# Revit family: Krome C8863-C8868 VS seris
name_source: partatom
category: Generic Models
revit_build: Autodesk Revit 2018 (Build: 20170223_1515(x64)
units: mm (PartAtom-declared; Revit-internal decimal feet)

## family parameters
Always vertical = Yes
Can host rebar = No
Cut with Voids When Loaded = No
Part Type = Normal
Room Calculation Point = No
Round Connector Dimension = Use Diameter
Shared = No
Work Plane-Based = No

## types (6) — shared parameters
Model = C8863-VS Series
URL = http://www.kromedispense.com

## per-type parameters (varying)
| type | Weight (lbs.) |
| C8864-VS-12" Ecoline Wall Mount Grab Bar Vibrant Stainless | 1.29 |
| C8863-VS-9" Ecoline Wall Mount Grab Bar Vibrant Stainless | 1.20 |
| C8865-VS-18" Ecoline Wall Mount Grab Bar Vibrant Stainless | 1.61 |
| C8866-VS-24" Ecoline Wall Mount Grab Bar Vibrant Stainless | 1.95 |
| C8867-VS-36" Ecoline Wall Mount Grab Bar Vibrant Stainless | 2.57 |
| C8868-VS-48" Ecoline Wall Mount Grab Bar Vibrant Stainless | 3.20 |

## geometry (parser evidence)
native form markers: Sweep x2
no freeform markers — native parametric forms only
